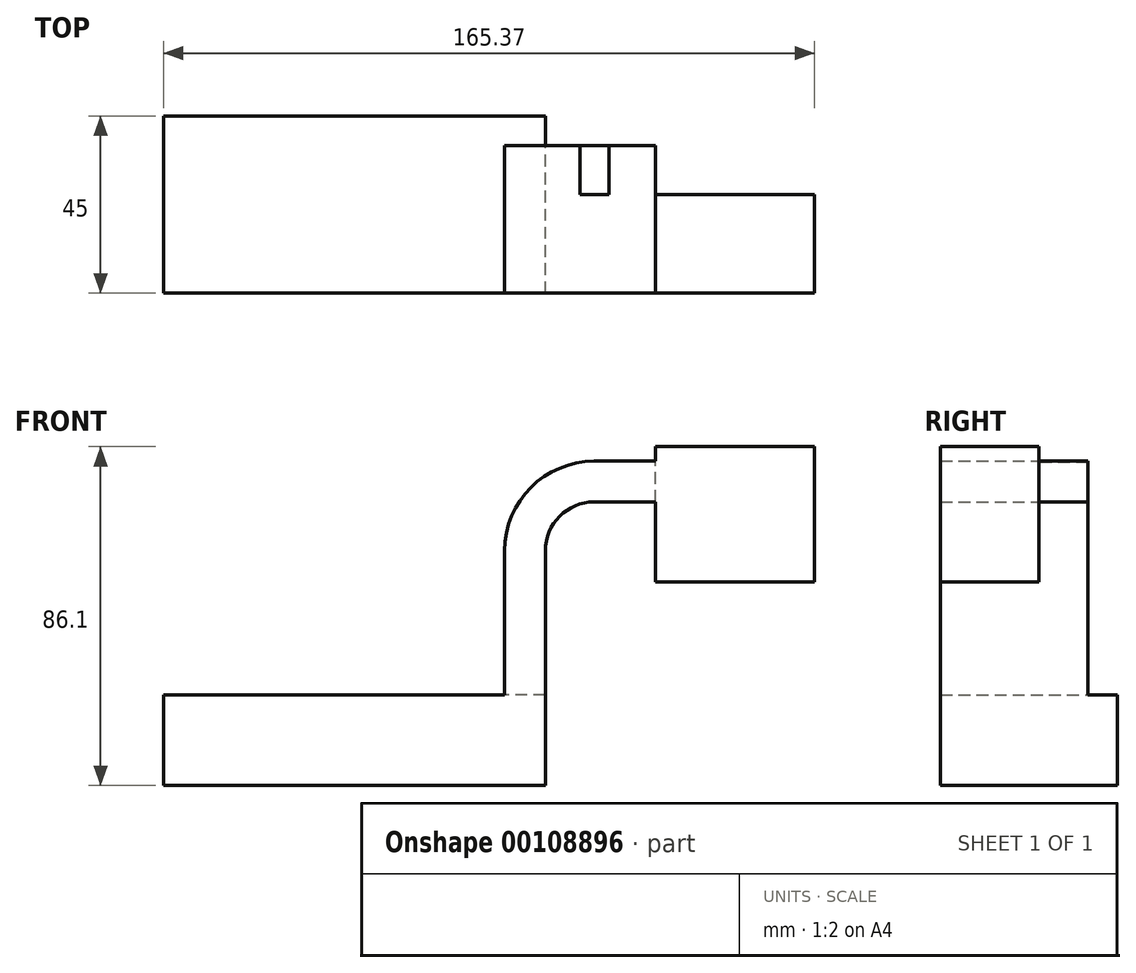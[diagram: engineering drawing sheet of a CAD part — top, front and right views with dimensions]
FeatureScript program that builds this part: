
annotation { "Feature Type Name" : "Feature", "Feature Type Description" : "" }
export const myFeature = defineFeature(function(context is Context, id is Id, definition is map)
    precondition{}
    {
        {
            var Q0;
            Q0=qCreatedBy(makeId("Front.planeOp"),FACE);
            var sketch = newSketch(context, id + "F0", { "sketchPlane" : qUnion([Q0])});
            skLineSegment(sketch, "E0.bottom", {"start": v(48.5, 11.5) * mm, "end": v(-48.5, 11.5) * mm});
            skLineSegment(sketch, "E0.top", {"start": v(48.5, -11.5) * mm, "end": v(-48.5, -11.5) * mm});
            skLineSegment(sketch, "E0.left", {"start": v(48.5, 11.5) * mm, "end": v(48.5, -11.5) * mm});
            skLineSegment(sketch, "E0.right", {"start": v(-48.5, 11.5) * mm, "end": v(-48.5, -11.5) * mm});
            skPoint(sketch, "E0.middle", {"position": v(0, 0) * mm});
            skLineSegment(sketch, "E1.bottom", {"start": v(116.87, 40.25) * mm, "end": v(76.45, 40.25) * mm});
            skLineSegment(sketch, "E1.top", {"start": v(116.87, 74.6) * mm, "end": v(76.45, 74.6) * mm});
            skLineSegment(sketch, "E1.left", {"start": v(116.87, 40.25) * mm, "end": v(116.87, 74.6) * mm});
            skLineSegment(sketch, "E1.right", {"start": v(76.45, 40.25) * mm, "end": v(76.45, 74.6) * mm});
            skPoint(sketch, "E1.middle", {"position": v(96.66, 57.43) * mm});
            skLineSegment(sketch, "E2", {"start": v(48.5, 11.5) * mm, "end": v(48.5, 48.11) * mm});
            skArc(sketch, "E3", {"start": v(48.5, 48.11) * mm, "mid": v(52.14, 56.9) * mm, "end": v(60.93, 60.54) * mm});
            skLineSegment(sketch, "E4", {"start": v(60.93, 60.54) * mm, "end": v(92.67, 60.54) * mm});
            skLineSegment(sketch, "E5.0", {"start": v(60.93, 70.9) * mm, "end": v(92.67, 70.9) * mm});
            skArc(sketch, "E5.1", {"start": v(38.15, 48.11) * mm, "mid": v(44.82, 64.22) * mm, "end": v(60.93, 70.9) * mm});
            skLineSegment(sketch, "E5.2", {"start": v(38.15, 11.5) * mm, "end": v(38.15, 48.11) * mm});
            skFitSpline(sketch, "E6", {"points": [v(-48.52, 11.91) * mm, v(64.7, 70.9) * mm], "startDerivative": vector(-12.1, 124.23) * mm, "endDerivative": vector(115, 1.82) * mm});
            skSolve(sketch);
        }
        {
            var Q0;
            Q0=makeQuery(id+"F0.imprint","IMPRINT",FACE,{"disambiguationData":[TD([[makeQuery(id+"F0.imprint","IMPRINT",EDGE,{"derivedFrom":sQuery(id+"F0.wireOp",EDGE,"E0.top")}),-1.0]])]});
            extrude(context, id + "F1", {"entities" : qUnion([Q0]), "endBound" : BoundingType.SYMMETRIC, "depth" : 40 * mm});
        }
        {
            var Q0;
            {var subQ5=sQuery(id+"F0.wireOp",EDGE,"E2");Q0=makeQuery(id+"F0.imprint","IMPRINT",FACE,{"disambiguationData":[TD([[makeQuery(id+"F0.imprint","IMPRINT",EDGE,{"derivedFrom":subQ5}),1.0]])]});}
            extrude(context, id + "F2", {"entities" : qUnion([Q0]), "operationType" : NewBodyOperationType.ADD, "endBound" : BoundingType.SYMMETRIC, "depth" : 25 * mm});
        }
        {
            var Q0;
            Q0 = qSketchRegion(id + "F0", true);
            extrude(context, id + "F3", {"entities" : qUnion([Q0]), "operationType" : NewBodyOperationType.ADD, "depth" : 25 * mm});
        }
        {
            var Q0;
            Q0 = qSketchRegion(id + "F0", true);
            extrude(context, id + "F4", {"entities" : qUnion([Q0]), "operationType" : NewBodyOperationType.ADD, "depth" : 25 * mm});
        }
    });
